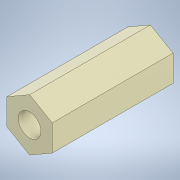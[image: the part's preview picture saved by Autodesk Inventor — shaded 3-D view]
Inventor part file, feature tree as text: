
AUTODESK INVENTOR PART (.ipt)
format: ipt  version: 2020.2 (Build 242310000, 310)  size: 98,304 bytes
history: native  units: mm
features: other x1, extrude x1, sketch x1
ambient origin geometry x8: Origin, YZ Plane, XZ Plane, XY Plane, X Axis, Y Axis, Z Axis, Center Point
bodies: Body1 (feature_tree)
feature tree (3):
  other  "ソリッド1"
  extrude  "押し出し1"  Depth=6.0mm
  sketch  "スケッチ1"
